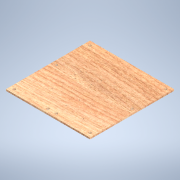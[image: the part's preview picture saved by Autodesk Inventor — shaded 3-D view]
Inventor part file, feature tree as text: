
AUTODESK INVENTOR PART (.ipt)
format: ipt  version: 2020 (Build 240168000, 168)  size: 212,992 bytes
history: native  units: in
note: dims shown in document units (in); Inventor stores cm internally (conversion verified against a paired STEP export)
features: extrude x7, sketch x7
ambient origin geometry x8: Origin, YZ Plane, XZ Plane, XY Plane, X Axis, Y Axis, Z Axis, Center Point
bodies: Solid1 (feature_tree)
feature tree (14):
  extrude  "Extrusion1"  Depth=8.0in
  extrude  "Extrusion2"  Depth=0.15in
  extrude  "Extrusion3"  Depth=0.15in TaperAngle=0.0deg
  extrude  "Extrusion4"  Depth=0.25in
  extrude  "Extrusion5"  Depth=0.15in TaperAngle=0.0deg
  extrude  "Extrusion6"  Depth=0.15in TaperAngle=0.0deg
  extrude  "Extrusion7"  Depth=0.15in
  sketch  "Sketch1"  dims[d0=8.0in d1=8.0in]
  sketch  "Sketch2"  dims[d2=0.15in d3=0.0in d4=0.8in]
  sketch  "Sketch3"  dims[d5=0.25in d6=0.15in d7=0.0in]
  sketch  "Sketch4"  dims[d8=0.8in d9=0.25in]
  sketch  "Sketch5"  dims[d10=0.8in d11=0.25in d12=0.15in d13=0.0in]
  sketch  "Sketch6"  dims[d14=4.25in d15=0.15in d16=0.0in]
  sketch  "Sketch7"  dims[d17=0.8in d18=0.25in d19=0.15in d20=0.0in d21=0.15in d22=0.0in d23=0.15in d24=0.0in]
